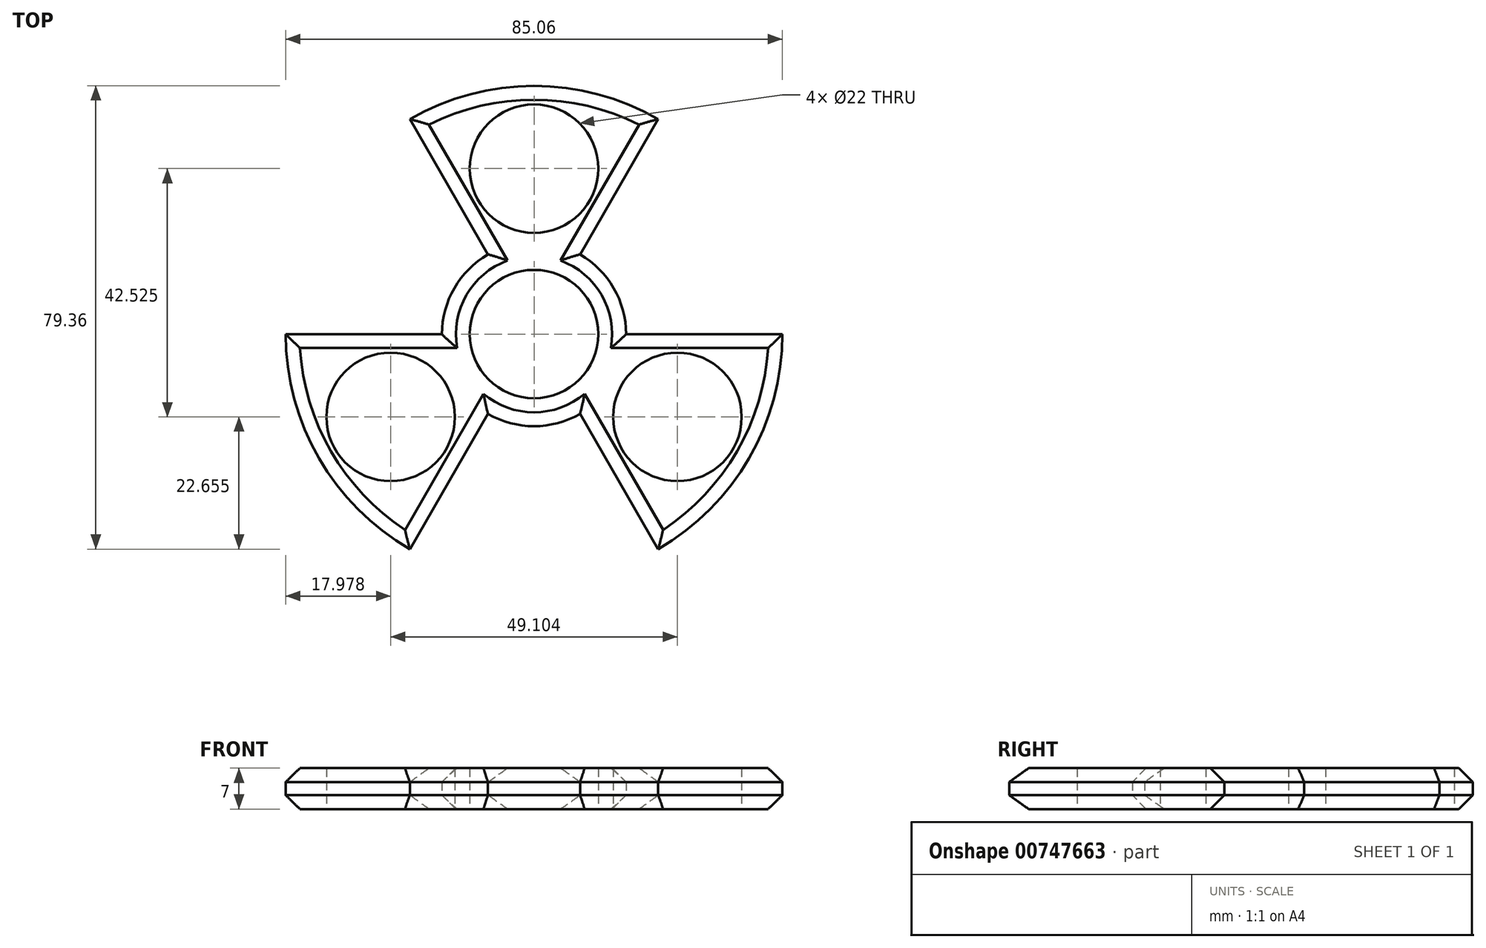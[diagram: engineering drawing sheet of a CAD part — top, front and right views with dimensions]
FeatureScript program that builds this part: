
annotation { "Feature Type Name" : "Feature", "Feature Type Description" : "" }
export const myFeature = defineFeature(function(context is Context, id is Id, definition is map)
    precondition{}
    {
        {
            var Q0;
            Q0=qCreatedBy(makeId("Top.planeOp"),FACE);
            var sketch = newSketch(context, id + "F0", { "sketchPlane" : qUnion([Q0])});
            skCircle(sketch, "E0", {"center": v(0, 0) * mm, "radius": 11 * mm});
            skCircle(sketch, "E1", {"center": v(0, 0) * mm, "radius": 15.76 * mm});
            skCircle(sketch, "E2", {"center": v(0, 0) * mm, "radius": 42.53 * mm});
            skLineSegment(sketch, "E3", {"start": v(0, 0) * mm, "end": v(21.26, 36.83) * mm});
            skLineSegment(sketch, "E4.1.0", {"start": v(0, 0) * mm, "end": v(42.53, 0) * mm});
            skLineSegment(sketch, "E4.2.0", {"start": v(0, 0) * mm, "end": v(21.26, -36.83) * mm});
            skLineSegment(sketch, "E4.3.0", {"start": v(0, 0) * mm, "end": v(-21.26, -36.83) * mm});
            skLineSegment(sketch, "E4.4.0", {"start": v(0, 0) * mm, "end": v(-42.53, 0) * mm});
            skLineSegment(sketch, "E4.5.0", {"start": v(0, 0) * mm, "end": v(-21.26, 36.83) * mm});
            skLineSegment(sketch, "E4.anchor1", {"start": v(0, 0) * mm, "end": v(21.26, 36.83) * mm, "construction": true});
            skLineSegment(sketch, "E4.anchor2", {"start": v(0, 0) * mm, "end": v(-21.26, 36.83) * mm, "construction": true});
            skCircle(sketch, "E5", {"center": v(0, 28.35) * mm, "radius": 14.18 * mm});
            skCircle(sketch, "E6", {"center": v(0, 28.35) * mm, "radius": 11 * mm});
            skCircle(sketch, "E7.1.0", {"center": v(-24.55, -14.18) * mm, "radius": 11 * mm});
            skCircle(sketch, "E7.2.0", {"center": v(24.55, -14.18) * mm, "radius": 11 * mm});
            skSolve(sketch);
        }
        {
            var Q0;
            {var subQ0=sQuery(id+"F0.wireOp",EDGE,"E3");var subQ1=sQuery(id+"F0.wireOp",EDGE,"E2");var subQ2=makeQuery(id+"F0.imprint","INTERSECT",VERTEX,{"derivedFrom":[subQ1,subQ0]});Q0=makeQuery(id+"F0.imprint","IMPRINT",FACE,{"disambiguationData":[TD([[makeQuery(id+"F0.imprint","IMPRINT",EDGE,{"disambiguationData":[TD([[subQ2,-1.0]])],"derivedFrom":subQ1}),1.0]])]});}
            var Q1;
            {var subQ0=sQuery(id+"F0.wireOp",EDGE,"E4.5.0");var subQ1=sQuery(id+"F0.wireOp",EDGE,"E2");var subQ2=makeQuery(id+"F0.imprint","INTERSECT",VERTEX,{"derivedFrom":[subQ1,subQ0]});Q1=makeQuery(id+"F0.imprint","IMPRINT",FACE,{"disambiguationData":[TD([[makeQuery(id+"F0.imprint","IMPRINT",EDGE,{"disambiguationData":[TD([[subQ2,1.0]])],"derivedFrom":subQ1}),1.0]])]});}
            var Q2;
            Q2=makeQuery(id+"F0.imprint","IMPRINT",FACE,{"disambiguationData":[TD([[makeQuery(id+"F0.imprint","IMPRINT",EDGE,{"derivedFrom":sQuery(id+"F0.wireOp",EDGE,"E7.1.0")}),-1.0]])]});
            var Q3;
            Q3=makeQuery(id+"F0.imprint","IMPRINT",FACE,{"disambiguationData":[TD([[makeQuery(id+"F0.imprint","IMPRINT",EDGE,{"derivedFrom":sQuery(id+"F0.wireOp",EDGE,"E7.2.0")}),-1.0]])]});
            var Q4;
            Q4=makeQuery(id+"F0.imprint","IMPRINT",FACE,{"disambiguationData":[TD([[makeQuery(id+"F0.imprint","IMPRINT",EDGE,{"derivedFrom":sQuery(id+"F0.wireOp",EDGE,"E6")}),-1.0]])]});
            var Q5;
            {var subQ0=sQuery(id+"F0.wireOp",EDGE,"E3");var subQ1=sQuery(id+"F0.wireOp",EDGE,"E1");var subQ2=makeQuery(id+"F0.imprint","INTERSECT",VERTEX,{"derivedFrom":[subQ1,subQ0]});Q5=makeQuery(id+"F0.imprint","IMPRINT",FACE,{"disambiguationData":[TD([[makeQuery(id+"F0.imprint","IMPRINT",EDGE,{"disambiguationData":[TD([[subQ2,-1.0]])],"derivedFrom":subQ1}),-1.0]])]});}
            var Q6;
            {var subQ0=sQuery(id+"F0.wireOp",EDGE,"E5");var subQ1=sQuery(id+"F0.wireOp",EDGE,"E1");var subQ2=makeQuery(id+"F0.imprint","INTERSECT",VERTEX,{"disambiguationData":[OD(0.0)],"derivedFrom":[subQ1,subQ0]});Q6=makeQuery(id+"F0.imprint","IMPRINT",FACE,{"disambiguationData":[TD([[makeQuery(id+"F0.imprint","IMPRINT",EDGE,{"disambiguationData":[TD([[subQ2,-1.0]])],"derivedFrom":subQ1}),1.0]])]});}
            var Q7;
            {var subQ0=sQuery(id+"F0.wireOp",EDGE,"E5");var subQ1=sQuery(id+"F0.wireOp",EDGE,"E1");var subQ2=makeQuery(id+"F0.imprint","INTERSECT",VERTEX,{"disambiguationData":[OD(1.0)],"derivedFrom":[subQ1,subQ0]});Q7=makeQuery(id+"F0.imprint","IMPRINT",FACE,{"disambiguationData":[TD([[makeQuery(id+"F0.imprint","IMPRINT",EDGE,{"disambiguationData":[TD([[subQ2,-1.0]])],"derivedFrom":subQ1}),-1.0]])]});}
            var Q8;
            {var subQ0=sQuery(id+"F0.wireOp",EDGE,"E4.1.0");var subQ1=sQuery(id+"F0.wireOp",EDGE,"E0");var subQ2=makeQuery(id+"F0.imprint","INTERSECT",VERTEX,{"derivedFrom":[subQ1,subQ0]});Q8=makeQuery(id+"F0.imprint","IMPRINT",FACE,{"disambiguationData":[TD([[makeQuery(id+"F0.imprint","IMPRINT",EDGE,{"disambiguationData":[TD([[subQ2,1.0]])],"derivedFrom":subQ1}),-1.0]])]});}
            var Q9;
            {var subQ0=sQuery(id+"F0.wireOp",EDGE,"E4.3.0");var subQ1=sQuery(id+"F0.wireOp",EDGE,"E0");var subQ2=makeQuery(id+"F0.imprint","INTERSECT",VERTEX,{"derivedFrom":[subQ1,subQ0]});Q9=makeQuery(id+"F0.imprint","IMPRINT",FACE,{"disambiguationData":[TD([[makeQuery(id+"F0.imprint","IMPRINT",EDGE,{"disambiguationData":[TD([[subQ2,-1.0]])],"derivedFrom":subQ1}),-1.0]])]});}
            var Q10;
            {var subQ0=sQuery(id+"F0.wireOp",EDGE,"E4.4.0");var subQ1=sQuery(id+"F0.wireOp",EDGE,"E0");var subQ2=makeQuery(id+"F0.imprint","INTERSECT",VERTEX,{"derivedFrom":[subQ1,subQ0]});Q10=makeQuery(id+"F0.imprint","IMPRINT",FACE,{"disambiguationData":[TD([[makeQuery(id+"F0.imprint","IMPRINT",EDGE,{"disambiguationData":[TD([[subQ2,-1.0]])],"derivedFrom":subQ1}),-1.0]])]});}
            var Q11;
            {var subQ0=sQuery(id+"F0.wireOp",EDGE,"E4.5.0");var subQ1=sQuery(id+"F0.wireOp",EDGE,"E0");var subQ2=makeQuery(id+"F0.imprint","INTERSECT",VERTEX,{"derivedFrom":[subQ1,subQ0]});Q11=makeQuery(id+"F0.imprint","IMPRINT",FACE,{"disambiguationData":[TD([[makeQuery(id+"F0.imprint","IMPRINT",EDGE,{"disambiguationData":[TD([[subQ2,-1.0]])],"derivedFrom":subQ1}),-1.0]])]});}
            var Q12;
            {var subQ5=sQuery(id+"F0.wireOp",EDGE,"E3");var subQ6=sQuery(id+"F0.wireOp",EDGE,"E0");var subQ7=makeQuery(id+"F0.imprint","INTERSECT",VERTEX,{"derivedFrom":[subQ6,subQ5]});Q12=makeQuery(id+"F0.imprint","IMPRINT",FACE,{"disambiguationData":[TD([[makeQuery(id+"F0.imprint","IMPRINT",EDGE,{"disambiguationData":[TD([[subQ7,-1.0]])],"derivedFrom":subQ6}),-1.0]])]});}
            var Q13;
            {var subQ0=sQuery(id+"F0.wireOp",EDGE,"E3");var subQ1=sQuery(id+"F0.wireOp",EDGE,"E0");var subQ2=makeQuery(id+"F0.imprint","INTERSECT",VERTEX,{"derivedFrom":[subQ1,subQ0]});Q13=makeQuery(id+"F0.imprint","IMPRINT",FACE,{"disambiguationData":[TD([[makeQuery(id+"F0.imprint","IMPRINT",EDGE,{"disambiguationData":[TD([[subQ2,1.0]])],"derivedFrom":subQ1}),-1.0]])]});}
            var Q14;
            {var subQ0=sQuery(id+"F0.wireOp",EDGE,"E3");var subQ1=sQuery(id+"F0.wireOp",EDGE,"E0");var subQ2=makeQuery(id+"F0.imprint","INTERSECT",VERTEX,{"derivedFrom":[subQ1,subQ0]});Q14=makeQuery(id+"F0.imprint","IMPRINT",FACE,{"disambiguationData":[TD([[makeQuery(id+"F0.imprint","IMPRINT",EDGE,{"disambiguationData":[TD([[subQ2,1.0]])],"derivedFrom":subQ1}),1.0]])]});}
            var Q15;
            {var subQ0=sQuery(id+"F0.wireOp",EDGE,"E3");var subQ1=sQuery(id+"F0.wireOp",EDGE,"E0");var subQ2=makeQuery(id+"F0.imprint","INTERSECT",VERTEX,{"derivedFrom":[subQ1,subQ0]});Q15=makeQuery(id+"F0.imprint","IMPRINT",FACE,{"disambiguationData":[TD([[makeQuery(id+"F0.imprint","IMPRINT",EDGE,{"disambiguationData":[TD([[subQ2,-1.0]])],"derivedFrom":subQ1}),1.0]])]});}
            var Q16;
            {var subQ0=sQuery(id+"F0.wireOp",EDGE,"E4.5.0");var subQ1=sQuery(id+"F0.wireOp",EDGE,"E0");var subQ2=makeQuery(id+"F0.imprint","INTERSECT",VERTEX,{"derivedFrom":[subQ1,subQ0]});Q16=makeQuery(id+"F0.imprint","IMPRINT",FACE,{"disambiguationData":[TD([[makeQuery(id+"F0.imprint","IMPRINT",EDGE,{"disambiguationData":[TD([[subQ2,-1.0]])],"derivedFrom":subQ1}),1.0]])]});}
            var Q17;
            {var subQ0=sQuery(id+"F0.wireOp",EDGE,"E4.4.0");var subQ1=sQuery(id+"F0.wireOp",EDGE,"E0");var subQ2=makeQuery(id+"F0.imprint","INTERSECT",VERTEX,{"derivedFrom":[subQ1,subQ0]});Q17=makeQuery(id+"F0.imprint","IMPRINT",FACE,{"disambiguationData":[TD([[makeQuery(id+"F0.imprint","IMPRINT",EDGE,{"disambiguationData":[TD([[subQ2,-1.0]])],"derivedFrom":subQ1}),1.0]])]});}
            var Q18;
            {var subQ0=sQuery(id+"F0.wireOp",EDGE,"E4.3.0");var subQ1=sQuery(id+"F0.wireOp",EDGE,"E0");var subQ2=makeQuery(id+"F0.imprint","INTERSECT",VERTEX,{"derivedFrom":[subQ1,subQ0]});Q18=makeQuery(id+"F0.imprint","IMPRINT",FACE,{"disambiguationData":[TD([[makeQuery(id+"F0.imprint","IMPRINT",EDGE,{"disambiguationData":[TD([[subQ2,-1.0]])],"derivedFrom":subQ1}),1.0]])]});}
            var Q19;
            {var subQ0=sQuery(id+"F0.wireOp",EDGE,"E4.1.0");var subQ1=sQuery(id+"F0.wireOp",EDGE,"E0");var subQ2=makeQuery(id+"F0.imprint","INTERSECT",VERTEX,{"derivedFrom":[subQ1,subQ0]});Q19=makeQuery(id+"F0.imprint","IMPRINT",FACE,{"disambiguationData":[TD([[makeQuery(id+"F0.imprint","IMPRINT",EDGE,{"disambiguationData":[TD([[subQ2,1.0]])],"derivedFrom":subQ1}),1.0]])]});}
            var Q20;
            Q20=makeQuery(id+"F0.imprint","IMPRINT",FACE,{"disambiguationData":[TD([[makeQuery(id+"F0.imprint","IMPRINT",EDGE,{"derivedFrom":sQuery(id+"F0.wireOp",EDGE,"E7.2.0")}),1.0]])]});
            var Q21;
            Q21=makeQuery(id+"F0.imprint","IMPRINT",FACE,{"disambiguationData":[TD([[makeQuery(id+"F0.imprint","IMPRINT",EDGE,{"derivedFrom":sQuery(id+"F0.wireOp",EDGE,"E6")}),1.0]])]});
            var Q22;
            Q22=makeQuery(id+"F0.imprint","IMPRINT",FACE,{"disambiguationData":[TD([[makeQuery(id+"F0.imprint","IMPRINT",EDGE,{"derivedFrom":sQuery(id+"F0.wireOp",EDGE,"E7.1.0")}),1.0]])]});
            extrude(context, id + "F1", {"entities" : qUnion([Q0, Q1, Q2, Q3, Q4, Q5, Q6, Q7, Q8, Q9, Q10, Q11, Q12, Q13, Q14, Q15, Q16, Q17, Q18, Q19, Q20, Q21, Q22]), "depth" : 7 * mm, "offsetDistance" : 25.4 * mm});
        }
        {
            var Q0;
            Q0=makeQuery(id+"F1.opExtrude","CAP_FACE",FACE,{"disambiguationData":[OSD([sQuery(id+"F0.wireOp",EDGE,"E1"),sQuery(id+"F0.wireOp",EDGE,"E2"),sQuery(id+"F0.wireOp",EDGE,"E3"),sQuery(id+"F0.wireOp",EDGE,"E4.1.0"),sQuery(id+"F0.wireOp",EDGE,"E4.2.0"),sQuery(id+"F0.wireOp",EDGE,"E4.3.0"),sQuery(id+"F0.wireOp",EDGE,"E4.4.0"),sQuery(id+"F0.wireOp",EDGE,"E4.5.0")])],"isStart":false});
            var Q1;
            Q1=makeQuery(id+"F1.opExtrude","CAP_FACE",FACE,{"disambiguationData":[OSD([sQuery(id+"F0.wireOp",EDGE,"E1"),sQuery(id+"F0.wireOp",EDGE,"E2"),sQuery(id+"F0.wireOp",EDGE,"E3"),sQuery(id+"F0.wireOp",EDGE,"E4.1.0"),sQuery(id+"F0.wireOp",EDGE,"E4.2.0"),sQuery(id+"F0.wireOp",EDGE,"E4.3.0"),sQuery(id+"F0.wireOp",EDGE,"E4.4.0"),sQuery(id+"F0.wireOp",EDGE,"E4.5.0")])],"isStart":true});
            chamfer(context, id + "F2", {"entities" : qUnion([Q0, Q1]), "width" : 2.38 * mm, "tangentPropagation" : true});
        }
        {
            var Q0;
            Q0=makeQuery(id+"F0.imprint","IMPRINT",FACE,{"disambiguationData":[TD([[makeQuery(id+"F0.imprint","IMPRINT",EDGE,{"derivedFrom":sQuery(id+"F0.wireOp",EDGE,"E7.2.0")}),1.0]])]});
            var Q1;
            Q1=makeQuery(id+"F0.imprint","IMPRINT",FACE,{"disambiguationData":[TD([[makeQuery(id+"F0.imprint","IMPRINT",EDGE,{"derivedFrom":sQuery(id+"F0.wireOp",EDGE,"E6")}),1.0]])]});
            var Q2;
            Q2=makeQuery(id+"F0.imprint","IMPRINT",FACE,{"disambiguationData":[TD([[makeQuery(id+"F0.imprint","IMPRINT",EDGE,{"derivedFrom":sQuery(id+"F0.wireOp",EDGE,"E7.1.0")}),1.0]])]});
            var Q3;
            {var subQ0=sQuery(id+"F0.wireOp",EDGE,"E4.1.0");var subQ1=sQuery(id+"F0.wireOp",EDGE,"E0");var subQ2=makeQuery(id+"F0.imprint","INTERSECT",VERTEX,{"derivedFrom":[subQ1,subQ0]});Q3=makeQuery(id+"F0.imprint","IMPRINT",FACE,{"disambiguationData":[TD([[makeQuery(id+"F0.imprint","IMPRINT",EDGE,{"disambiguationData":[TD([[subQ2,1.0]])],"derivedFrom":subQ1}),1.0]])]});}
            var Q4;
            {var subQ0=sQuery(id+"F0.wireOp",EDGE,"E3");var subQ1=sQuery(id+"F0.wireOp",EDGE,"E0");var subQ2=makeQuery(id+"F0.imprint","INTERSECT",VERTEX,{"derivedFrom":[subQ1,subQ0]});Q4=makeQuery(id+"F0.imprint","IMPRINT",FACE,{"disambiguationData":[TD([[makeQuery(id+"F0.imprint","IMPRINT",EDGE,{"disambiguationData":[TD([[subQ2,1.0]])],"derivedFrom":subQ1}),1.0]])]});}
            var Q5;
            {var subQ0=sQuery(id+"F0.wireOp",EDGE,"E3");var subQ1=sQuery(id+"F0.wireOp",EDGE,"E0");var subQ2=makeQuery(id+"F0.imprint","INTERSECT",VERTEX,{"derivedFrom":[subQ1,subQ0]});Q5=makeQuery(id+"F0.imprint","IMPRINT",FACE,{"disambiguationData":[TD([[makeQuery(id+"F0.imprint","IMPRINT",EDGE,{"disambiguationData":[TD([[subQ2,-1.0]])],"derivedFrom":subQ1}),1.0]])]});}
            var Q6;
            {var subQ0=sQuery(id+"F0.wireOp",EDGE,"E4.5.0");var subQ1=sQuery(id+"F0.wireOp",EDGE,"E0");var subQ2=makeQuery(id+"F0.imprint","INTERSECT",VERTEX,{"derivedFrom":[subQ1,subQ0]});Q6=makeQuery(id+"F0.imprint","IMPRINT",FACE,{"disambiguationData":[TD([[makeQuery(id+"F0.imprint","IMPRINT",EDGE,{"disambiguationData":[TD([[subQ2,-1.0]])],"derivedFrom":subQ1}),1.0]])]});}
            var Q7;
            {var subQ0=sQuery(id+"F0.wireOp",EDGE,"E4.4.0");var subQ1=sQuery(id+"F0.wireOp",EDGE,"E0");var subQ2=makeQuery(id+"F0.imprint","INTERSECT",VERTEX,{"derivedFrom":[subQ1,subQ0]});Q7=makeQuery(id+"F0.imprint","IMPRINT",FACE,{"disambiguationData":[TD([[makeQuery(id+"F0.imprint","IMPRINT",EDGE,{"disambiguationData":[TD([[subQ2,-1.0]])],"derivedFrom":subQ1}),1.0]])]});}
            var Q8;
            {var subQ0=sQuery(id+"F0.wireOp",EDGE,"E4.3.0");var subQ1=sQuery(id+"F0.wireOp",EDGE,"E0");var subQ2=makeQuery(id+"F0.imprint","INTERSECT",VERTEX,{"derivedFrom":[subQ1,subQ0]});Q8=makeQuery(id+"F0.imprint","IMPRINT",FACE,{"disambiguationData":[TD([[makeQuery(id+"F0.imprint","IMPRINT",EDGE,{"disambiguationData":[TD([[subQ2,-1.0]])],"derivedFrom":subQ1}),1.0]])]});}
            extrude(context, id + "F3", {"entities" : qUnion([Q0, Q1, Q2, Q3, Q4, Q5, Q6, Q7, Q8]), "operationType" : NewBodyOperationType.REMOVE, "depth" : 25.4 * mm, "offsetDistance" : 25.4 * mm});
        }
    });
